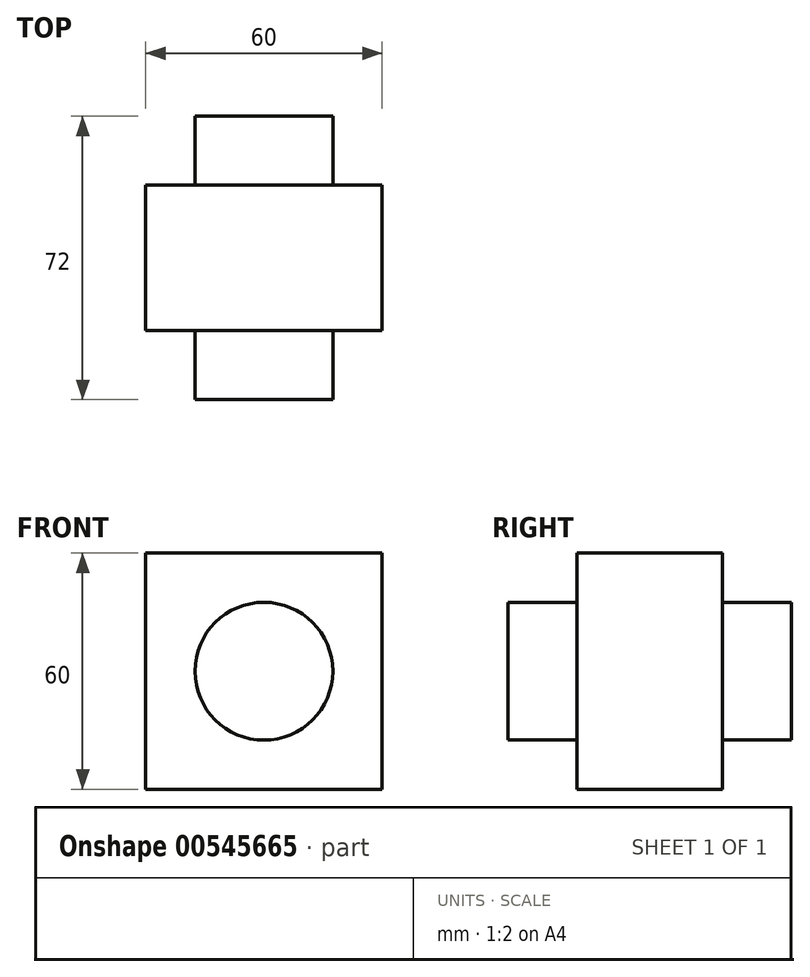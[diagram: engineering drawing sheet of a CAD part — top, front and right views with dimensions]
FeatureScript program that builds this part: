
annotation { "Feature Type Name" : "Feature", "Feature Type Description" : "" }
export const myFeature = defineFeature(function(context is Context, id is Id, definition is map)
    precondition{}
    {
        {
            var Q0;
            Q0=qCreatedBy(makeId("Front.planeOp"),FACE);
            var sketch = newSketch(context, id + "F0", { "sketchPlane" : qUnion([Q0])});
            skLineSegment(sketch, "E0.bottom", {"start": v(-30, 30) * mm, "end": v(30, 30) * mm});
            skLineSegment(sketch, "E0.top", {"start": v(-30, -30) * mm, "end": v(30, -30) * mm});
            skLineSegment(sketch, "E0.left", {"start": v(-30, 30) * mm, "end": v(-30, -30) * mm});
            skLineSegment(sketch, "E0.right", {"start": v(30, 30) * mm, "end": v(30, -30) * mm});
            skSolve(sketch);
        }
        {
            var Q0;
            Q0=makeQuery(id+"F0.imprint","IMPRINT",FACE,{"disambiguationData":[TD([[makeQuery(id+"F0.imprint","IMPRINT",EDGE,{"derivedFrom":sQuery(id+"F0.wireOp",EDGE,"E0.bottom")}),-1.0]])]});
            extrude(context, id + "F1", {"entities" : qUnion([Q0]), "depth" : 37 * mm, "offsetDistance" : 25 * mm, "symmetric" : true});
        }
        {
            var Q0;
            Q0=makeQuery(id+"F1.opExtrude","CAP_FACE",FACE,{"disambiguationData":[OSD([sQuery(id+"F0.wireOp",EDGE,"E0.bottom"),sQuery(id+"F0.wireOp",EDGE,"E0.top"),sQuery(id+"F0.wireOp",EDGE,"E0.left"),sQuery(id+"F0.wireOp",EDGE,"E0.right")])],"isStart":false});
            var sketch = newSketch(context, id + "F2", { "sketchPlane" : qUnion([Q0])});
            skCircle(sketch, "E1", {"center": v(0, 0) * mm, "radius": 17.5 * mm});
            skSolve(sketch);
        }
        {
            var Q0;
            Q0=makeQuery(id+"F1.opExtrude","CAP_FACE",FACE,{"disambiguationData":[OSD([sQuery(id+"F0.wireOp",EDGE,"E0.bottom"),sQuery(id+"F0.wireOp",EDGE,"E0.top"),sQuery(id+"F0.wireOp",EDGE,"E0.left"),sQuery(id+"F0.wireOp",EDGE,"E0.right")])],"isStart":true});
            var sketch = newSketch(context, id + "F3", { "sketchPlane" : qUnion([Q0])});
            skCircle(sketch, "E2", {"center": v(0, 0) * mm, "radius": 17.5 * mm});
            skSolve(sketch);
        }
        {
            var Q0;
            Q0 = qSketchRegion(id + "F2", true);
            extrude(context, id + "F4", {"entities" : qUnion([Q0]), "operationType" : NewBodyOperationType.ADD, "depth" : 17.5 * mm, "offsetDistance" : 25 * mm});
        }
        {
            var Q0;
            Q0 = qSketchRegion(id + "F3", true);
            extrude(context, id + "F5", {"entities" : qUnion([Q0]), "operationType" : NewBodyOperationType.ADD, "depth" : 17.5 * mm, "offsetDistance" : 25 * mm});
        }
    });
